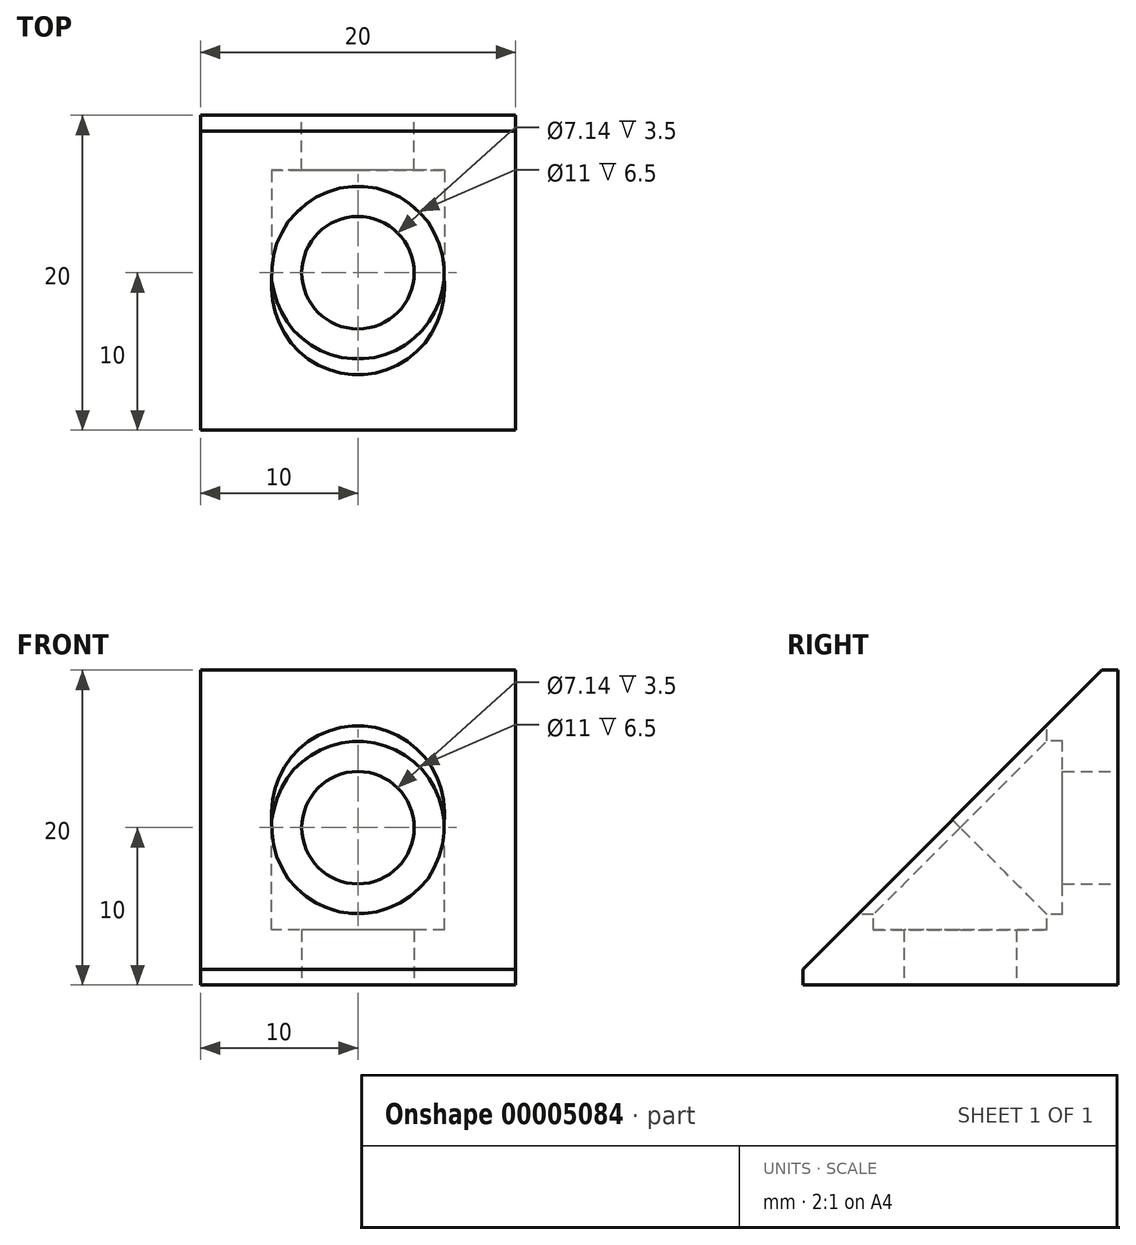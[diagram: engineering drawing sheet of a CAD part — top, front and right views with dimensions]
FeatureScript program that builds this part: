
annotation { "Feature Type Name" : "Feature", "Feature Type Description" : "" }
export const myFeature = defineFeature(function(context is Context, id is Id, definition is map)
    precondition{}
    {
        {
            var Q0;
            Q0=qCreatedBy(makeId("Front.planeOp"),FACE);
            var sketch = newSketch(context, id + "F0", { "sketchPlane" : qUnion([Q0])});
            skLineSegment(sketch, "E0.rect.bottom", {"start": v(10, 10) * mm, "end": v(-10, 10) * mm});
            skLineSegment(sketch, "E0.rect.top", {"start": v(10, -10) * mm, "end": v(-10, -10) * mm});
            skLineSegment(sketch, "E0.rect.left", {"start": v(10, 10) * mm, "end": v(10, -10) * mm});
            skLineSegment(sketch, "E0.rect.right", {"start": v(-10, 10) * mm, "end": v(-10, -10) * mm});
            skPoint(sketch, "E0.rect.middle", {"position": v(0, 0) * mm});
            skCircle(sketch, "E1", {"center": v(0, 0) * mm, "radius": 3.57 * mm});
            skSolve(sketch);
        }
        {
            var Q0;
            Q0=makeQuery(id+"F0.imprint","IMPRINT",FACE,{"disambiguationData":[TD([[makeQuery(id+"F0.imprint","IMPRINT",EDGE,{"derivedFrom":sQuery(id+"F0.wireOp",EDGE,"E0.rect.bottom")}),1.0]])]});
            extrude(context, id + "F1", {"entities" : qUnion([Q0]), "depth" : 20 * mm});
        }
        {
            var Q0;
            Q0=makeQuery(id+"F1.opExtrude","SWEPT_FACE",FACE,{"disambiguationData":[OSD([sQuery(id+"F0.wireOp",EDGE,"E0.rect.top")])]});
            var sketch = newSketch(context, id + "F2", { "sketchPlane" : qUnion([Q0])});
            skCircle(sketch, "E2", {"center": v(0, 10) * mm, "radius": 3.57 * mm});
            skSolve(sketch);
        }
        {
            var Q0;
            Q0=qSketchRegion(id+"F2",true);
            extrude(context, id + "F3", {"entities" : qUnion([Q0]), "operationType" : NewBodyOperationType.REMOVE, "endBound" : BoundingType.THROUGH_ALL, "oppositeDirection" : true, "depth" : 25 * mm});
        }
        {
            var Q0;
            Q0=makeQuery(id+"F1.opExtrude","SWEPT_FACE",FACE,{"disambiguationData":[OSD([sQuery(id+"F0.wireOp",EDGE,"E0.rect.right")])]});
            var sketch = newSketch(context, id + "F4", { "sketchPlane" : qUnion([Q0])});
            skLineSegment(sketch, "E3", {"start": v(20, 10) * mm, "end": v(1, 10) * mm});
            skLineSegment(sketch, "E4", {"start": v(20, 10) * mm, "end": v(20, -9) * mm});
            skLineSegment(sketch, "E5", {"start": v(20, -9) * mm, "end": v(1, 10) * mm});
            skSolve(sketch);
        }
        {
            var Q0;
            Q0=makeQuery(id+"F1.opExtrude","CAP_FACE",FACE,{"disambiguationData":[OSD([sQuery(id+"F0.wireOp",EDGE,"E0.rect.bottom"),sQuery(id+"F0.wireOp",EDGE,"E0.rect.top"),sQuery(id+"F0.wireOp",EDGE,"E0.rect.left"),sQuery(id+"F0.wireOp",EDGE,"E0.rect.right"),sQuery(id+"F0.wireOp",EDGE,"E1")])],"isStart":false});
            var sketch = newSketch(context, id + "F5", { "sketchPlane" : qUnion([Q0])});
            skCircle(sketch, "E6", {"center": v(0, 0) * mm, "radius": 5.5 * mm});
            skSolve(sketch);
        }
        {
            var Q0;
            Q0=qSketchRegion(id+"F5",true);
            extrude(context, id + "F6", {"entities" : qUnion([Q0]), "operationType" : NewBodyOperationType.REMOVE, "oppositeDirection" : true, "depth" : 16.5 * mm});
        }
        {
            var Q0;
            Q0=makeQuery(id+"F1.opExtrude","SWEPT_FACE",FACE,{"disambiguationData":[OSD([sQuery(id+"F0.wireOp",EDGE,"E0.rect.bottom")])]});
            var sketch = newSketch(context, id + "F7", { "sketchPlane" : qUnion([Q0])});
            skCircle(sketch, "E7", {"center": v(0, -10) * mm, "radius": 5.5 * mm});
            skSolve(sketch);
        }
        {
            var Q0;
            Q0=qSketchRegion(id+"F7",true);
            extrude(context, id + "F8", {"entities" : qUnion([Q0]), "operationType" : NewBodyOperationType.REMOVE, "oppositeDirection" : true, "depth" : 16.5 * mm});
        }
        {
            var Q0;
            Q0=qSketchRegion(id+"F4",true);
            extrude(context, id + "F9", {"entities" : qUnion([Q0]), "operationType" : NewBodyOperationType.REMOVE, "endBound" : BoundingType.THROUGH_ALL, "oppositeDirection" : true, "depth" : 25 * mm});
        }
    });
